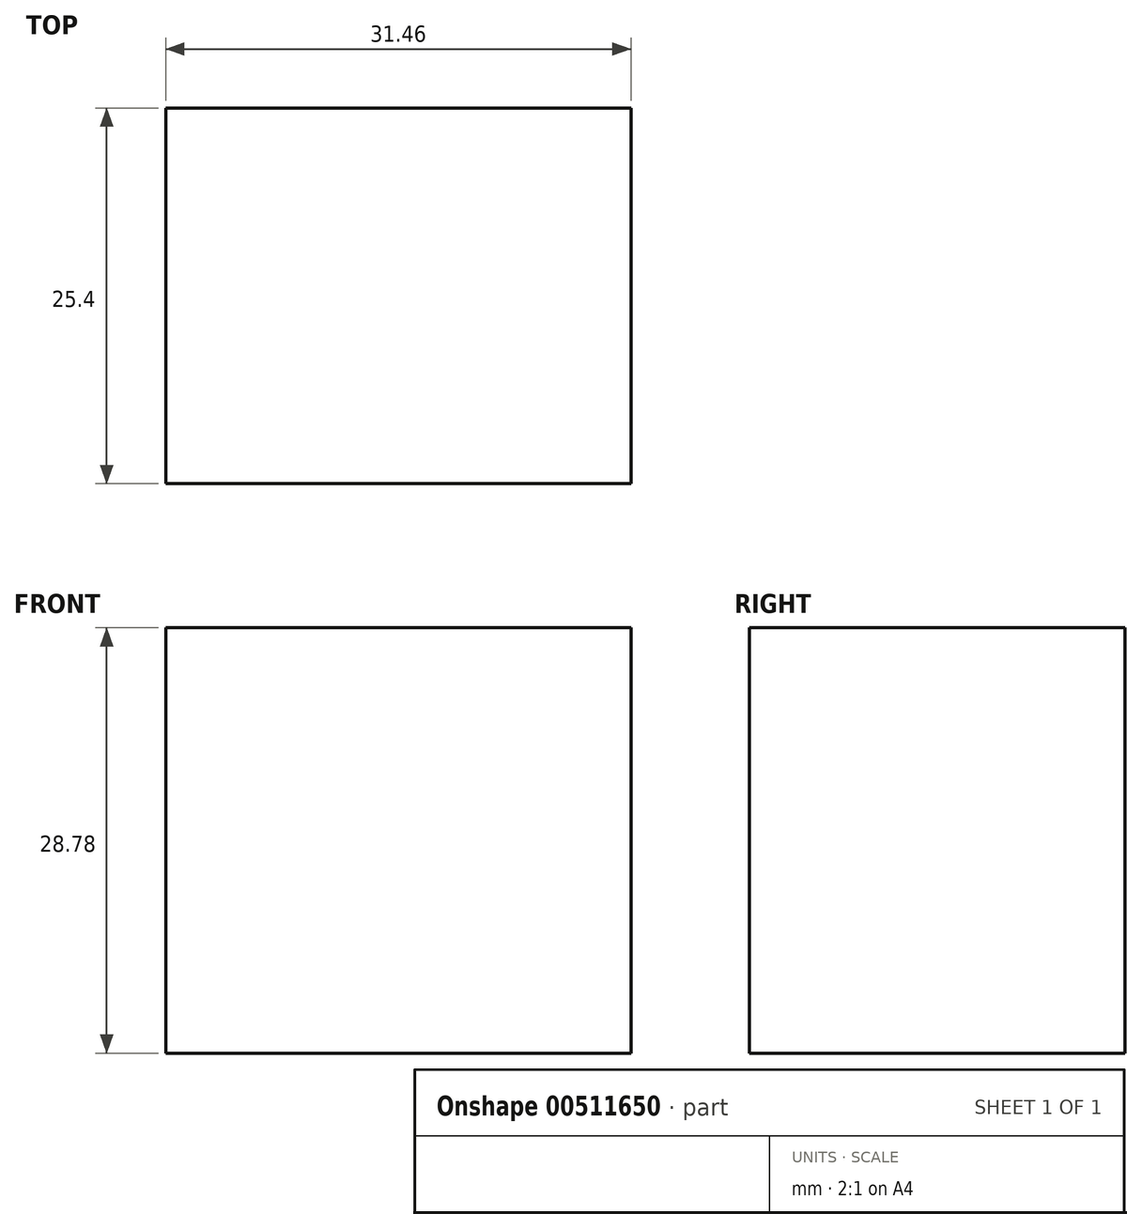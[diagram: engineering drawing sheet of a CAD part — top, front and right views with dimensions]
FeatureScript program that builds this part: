
annotation { "Feature Type Name" : "Feature", "Feature Type Description" : "" }
export const myFeature = defineFeature(function(context is Context, id is Id, definition is map)
    precondition{}
    {
        {
            var Q0;
            Q0=qCreatedBy(makeId("Front.planeOp"),FACE);
            var sketch = newSketch(context, id + "F0", { "sketchPlane" : qUnion([Q0])});
            skLineSegment(sketch, "E0.bottom", {"start": v(15.73, 14.64) * mm, "end": v(-15.73, 14.64) * mm});
            skLineSegment(sketch, "E0.top", {"start": v(15.73, -14.64) * mm, "end": v(-15.73, -14.64) * mm});
            skLineSegment(sketch, "E0.left", {"start": v(15.73, 14.64) * mm, "end": v(15.73, -14.64) * mm});
            skLineSegment(sketch, "E0.right", {"start": v(-15.73, 14.64) * mm, "end": v(-15.73, -14.64) * mm});
            skPoint(sketch, "E0.middle", {"position": v(0, 0) * mm});
            skSolve(sketch);
        }
        {
            var Q0;
            Q0 = qSketchRegion(id + "F0", true);
            extrude(context, id + "F1", {"entities" : qUnion([Q0]), "depth" : 25.4 * mm});
        }
        {
            var Q0;
            Q0=makeQuery(id+"F1.opExtrude","SWEPT_FACE",FACE,{"disambiguationData":[OSD([sQuery(id+"F0.wireOp",EDGE,"E0.bottom")])]});
            extrude(context, id + "F2", {"entities" : qUnion([Q0]), "operationType" : NewBodyOperationType.REMOVE, "oppositeDirection" : true, "depth" : 0.5 * mm, "hasDraft" : true, "draftAngle" : 30 * degree});
        }
    });
